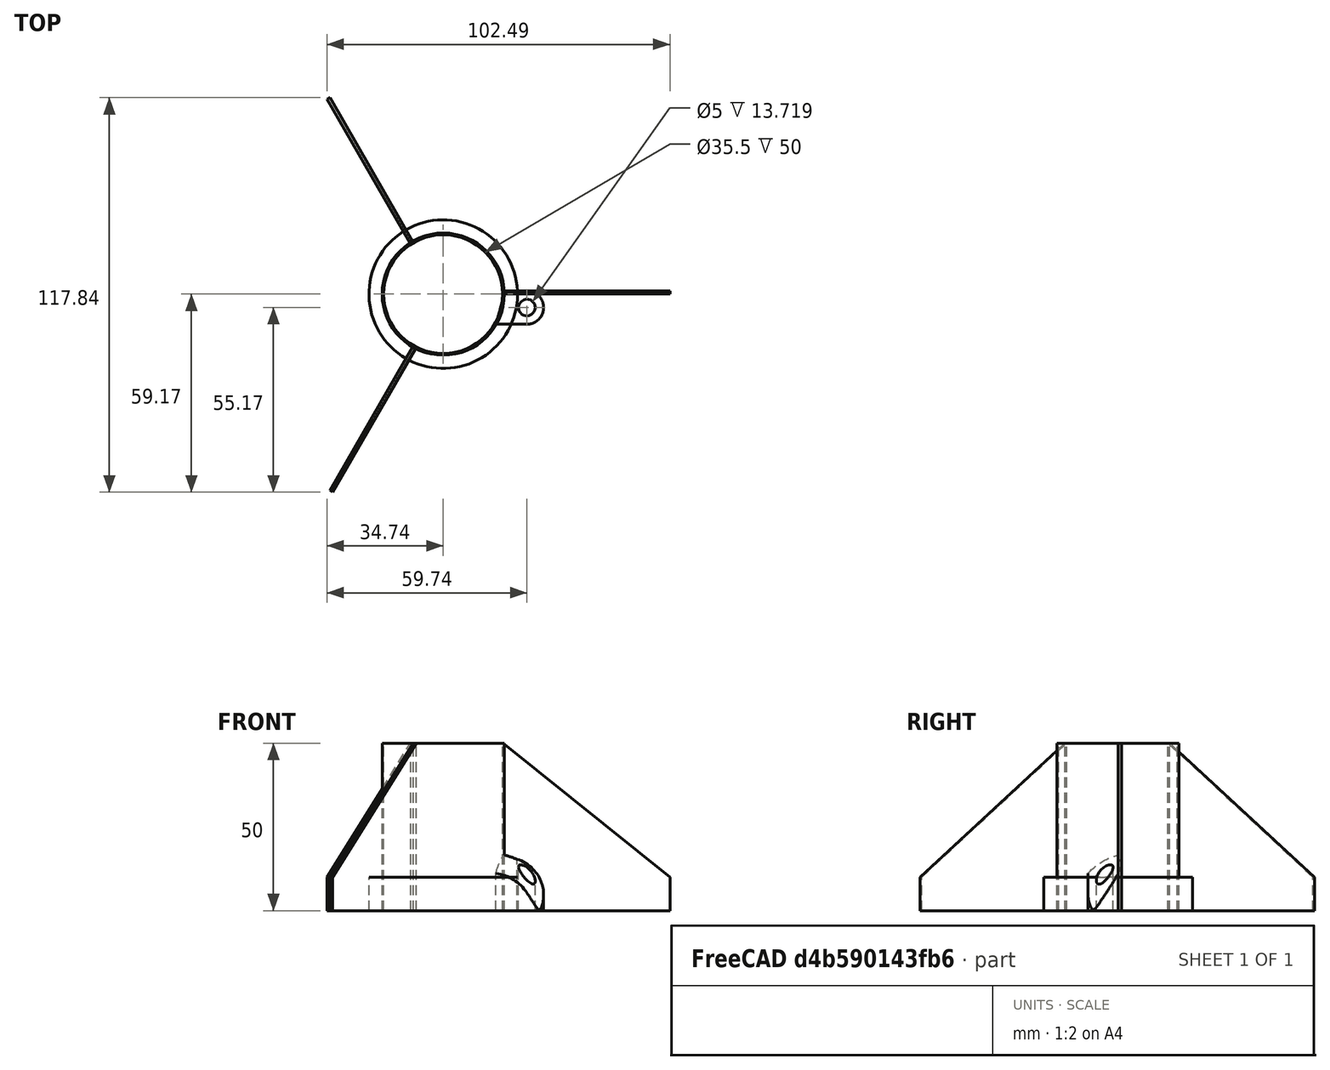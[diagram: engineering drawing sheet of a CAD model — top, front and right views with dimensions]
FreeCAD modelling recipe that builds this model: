
FCSTD DOCUMENT  (FreeCAD 0.18R4 (GitTag))
Label: fli3d fins v1.1
License: All rights reserved
LicenseURL: http://en.wikipedia.org/wiki/All_rights_reserved
objects: Part::Cylinder×5, Part::Box×4, Part::Chamfer×4, Part::Cut×2, Part::MultiFuse×1, Part::Sphere×1, Part::MultiCommon×1
note: 18 computed .brp shape members not serialized (recipe doc carries the construction recipe); baked Part::Feature solids carry a one-line shape summary decoded from their .brp

FEATURE [Part::Cylinder] Cylinder
  Angle = 360
  AttacherType = Attacher::AttachEngine3D
  Height = 50
  Radius = 18.25
FEATURE [Part::Cylinder] Cylinder001
  Angle = 360
  AttacherType = Attacher::AttachEngine3D
  Height = 50
  Radius = 17.75
FEATURE [Part::Cut] Cut  label="Tube"
  Base = -> Cylinder
  Tool = -> Cylinder001
FEATURE [Part::Box] Box  label="Cube"
  AttacherType = Attacher::AttachEngine3D
  Height = 50
  Length = 50
  Placement = pos=(17.75,0,0) rot=(0,0,1;0rad)
  Width = 1
FEATURE [Part::Cylinder] Cylinder002  label="Nosecone diameter reference"
  Angle = 360
  AttacherType = Attacher::AttachEngine3D
  Height = 10
  Radius = 22.2
FEATURE [Part::Cylinder] Cylinder003
  Angle = 360
  AttacherType = Attacher::AttachEngine3D
  Height = 50
  Placement = pos=(25,-4,0) rot=(0,0,1;0rad)
  Radius = 5
FEATURE [Part::Cylinder] Cylinder004
  Angle = 360
  AttacherType = Attacher::AttachEngine3D
  Height = 50
  Placement = pos=(25,-4,0) rot=(0,0,1;0rad)
  Radius = 2.5
FEATURE [Part::Box] Box001  label="Cube001"
  AttacherType = Attacher::AttachEngine3D
  Height = 50
  Length = 9.25
  Placement = pos=(15.75,-9,0) rot=(0,0,1;0rad)
  Width = 9
FEATURE [Part::Chamfer] Chamfer
  Base = -> Box001
  Edges = 1 edges: [Edge3 r1=8.9 r2=2.5]
FEATURE [Part::MultiFuse] Fusion
  Shapes = -> [Cylinder003,Chamfer]
FEATURE [Part::Chamfer] Chamfer001  label="Fin 001"
  Base = -> Box
  Edges = 1 edges: [Edge6 r1=40 r2=49.9]
FEATURE [Part::Box] Box002  label="Cube002"
  AttacherType = Attacher::AttachEngine3D
  Height = 50
  Length = 50
  Placement = pos=(17.75,0,0) rot=(0,0,1;0rad)
  Width = 1
FEATURE [Part::Chamfer] Chamfer002  label="Fin 002"
  Base = -> Box002
  Edges = 1 edges: [Edge6 r1=40 r2=49.9]
  Placement = pos=(0,0,0) rot=(0,0,1;2.0944rad)
FEATURE [Part::Box] Box003  label="Cube003"
  AttacherType = Attacher::AttachEngine3D
  Height = 50
  Length = 50
  Placement = pos=(17.75,0,0) rot=(0,0,1;0rad)
  Width = 1
FEATURE [Part::Chamfer] Chamfer003  label="Fin 003"
  Base = -> Box003
  Edges = 1 edges: [Edge6 r1=40 r2=49.9]
  Placement = pos=(0,0,0) rot=(0,0,1;4.18879rad)
FEATURE [Part::Sphere] Sphere
  Angle1 = -90
  Angle2 = 90
  Angle3 = 360
  AttacherType = Attacher::AttachEngine3D
  Placement = pos=(14,6,-2) rot=(0,0,1;0rad)
  Radius = 20
FEATURE [Part::MultiCommon] Common
  Shapes = -> [Fusion,Sphere]
FEATURE [Part::Cut] Cut001  label="Slider"
  Base = -> Common
  Tool = -> Cylinder004
